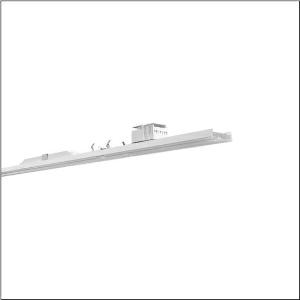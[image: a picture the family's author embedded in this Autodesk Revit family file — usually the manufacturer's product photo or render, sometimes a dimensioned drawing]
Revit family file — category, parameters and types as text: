
# Revit family: licross_r__21_recessed_mo_52tl18dne75f_0d69
name_source: partatom
category: Lighting Fixtures
units: mm (PartAtom-declared; Revit-internal decimal feet)

## family parameters
Cut with Voids When Loaded = No
Host = Face
Light Source = No
Part Type = Normal
Room Calculation Point = No
Round Connector Dimension = Use Diameter
Shared = No

## types (1)
- --- (1 x LED, 7740 lm, 61.1 W, 5000K)
    Apparent Load = 61 VA
    CIE Flux Codes = 79 95 99 100 100
    Color Rendering = 90
    Color Temperature = 5000K
    Default Elevation = 1800 mm
    Description = Licross® 21 Recessed MO, luminaire insert, of sheet steel, galvanised, coil coated, white, length: 1.500mm, width: 66mm, height: 67mm, LED rated luminous flux: 7.740lm, light colour: 950, control gear: DALI 2, control gear: ECG DALI, with plug, 5-pole, with phase selection, mains connection: 220..240V, AC, 50/60Hz, rated input power: 61W, halogen-free wiring, primary optical cover: cover, of PMMA, light emission: direct distribution, primary light characteristic: symmetric, protection rating (complete): IP40, insulation class (complete): insulation class I (protective earthing), certification: CE, ENEC, VDE, UKCA, protection symbol: D if used in an environment without relevant dust loads with corresponding accessories, impact resistance: IK06, permissible ambient temperature for indoor applications: -25..+35°C, corresponds to IFS (International Featured Standards) requirements for safety and quality in the food industry, reducing of maximum allowable ambient temperature of 5°C with ceiling mounting, LABS conformity tested according to VDMA 24364:2018-05, packaging unit: 1 piece
    Height = 58 mm
    Lamp = 1 x LED
    Lamp Light Flux = 7740 lm
    Lamp Power = 61.1 W
    Lamp count = 1
    Length = 1500 mm
    Luminous efficacy = 127 lm/W
    Manufacturer = Siteco
    ModVariant = No
    Model = 52TL18DNE75F
    Mounting Place = Ceiling
    Mounting Type = Pendant
    Number of Poles = 1
    OnlyDefault = Yes
    Power Factor = 1
    Product Name = Licross® 21 Recessed MO
    Product group = luminaire insert
    ProductGroupID = 901
    Protection Class = Protection class I
    Protection Degree = IP 40
    RLX_Detail_Level = 1
    RLX_Emergency_Light_Flux = 0 lm
    RLX_Emergency_Type = 0
    RLX_Emergency_Type_DB = No
    RlxData = <blob elided: 22665 chars, md5=6215a5d6>
    Socket = socket
    Standby Power = 0 W
    System Light Flux = 7740 lm
    System Power = 61 W
    Type Comments = factory setting: luminous flux: 100 % | dim-lin: 254 | 405 mA
    Type Image = l_1296935.jpg
    URL = http://relux.com
    VarID = @adj_135813
    Voltage = 0 V
    Weight = 0.00 kg
    Width = 66 mm

## geometry (parser evidence)
native form markers: Blend x4, Sweep x11
no freeform markers — native parametric forms only
